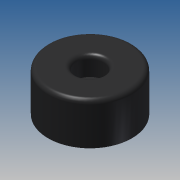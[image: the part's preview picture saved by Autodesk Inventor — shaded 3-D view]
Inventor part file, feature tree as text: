
AUTODESK INVENTOR PART (.ipt)
format: ipt  version: 2013 (Build 170138000, 138)  size: 110,592 bytes
history: native  units: mm
features: extrude x3, sketch x3, fillet x1
ambient origin geometry x8: Origin, YZ Plane, XZ Plane, XY Plane, X Axis, Y Axis, Z Axis, Center Point
bodies: Solid1 (feature_tree)
feature tree (7):
  extrude  "Extrusion1"  Depth=20.0mm TaperAngle=0.0deg
  extrude  "Extrusion2"  Depth=9.17mm TaperAngle=0.0deg
  extrude  "Extrusion3"  Depth=9.17mm TaperAngle=0.0deg
  fillet  "Fillet1"  Radius=2.0mm
  sketch  "Sketch1"  dims[d0=40.0mm d2=20.0mm d3=0.0mm]
  sketch  "Sketch2"  dims[d4=13.0mm d6=9.17mm d7=0.0mm]
  sketch  "Sketch3"  dims[d8=6.5mm d10=9.17mm d11=0.0mm d12=2.0mm]
